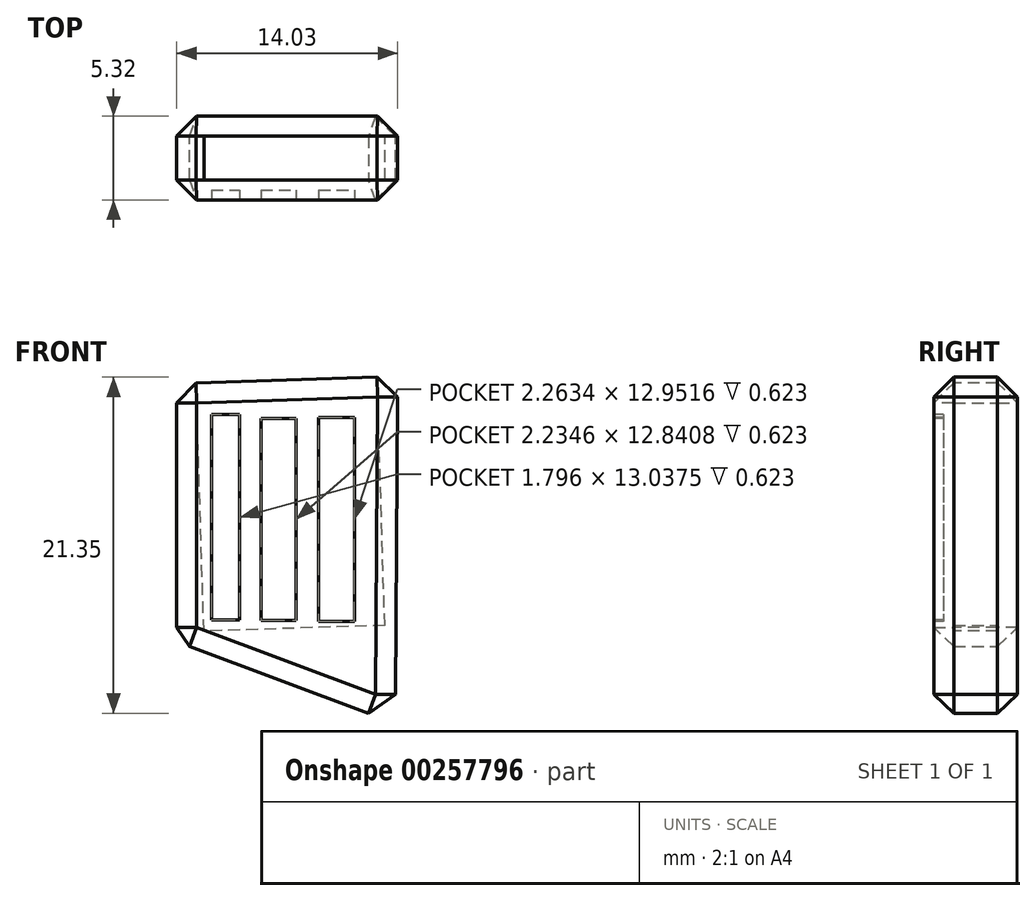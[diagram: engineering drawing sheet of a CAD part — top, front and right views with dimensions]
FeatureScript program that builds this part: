
annotation { "Feature Type Name" : "Feature", "Feature Type Description" : "" }
export const myFeature = defineFeature(function(context is Context, id is Id, definition is map)
    precondition{}
    {
        {
            var Q0;
            Q0=qCreatedBy(makeId("Front.planeOp"),FACE);
            var sketch = newSketch(context, id + "F4", { "sketchPlane" : qUnion([Q0])});
            skLineSegment(sketch, "E0", {"start": v(-13.89, 0) * mm, "end": v(-13.89, -16.38) * mm});
            skLineSegment(sketch, "E1", {"start": v(-13.89, -16.38) * mm, "end": v(0, -21.59) * mm});
            skLineSegment(sketch, "E2", {"start": v(0, -21.59) * mm, "end": v(0.15, 0.44) * mm});
            skLineSegment(sketch, "E3", {"start": v(0.15, 0.44) * mm, "end": v(-13.89, 0) * mm});
            skSolve(sketch);
        }
        {
            var Q0;
            Q0=qSketchRegion(id+"F4",true);
            extrude(context, id + "F0", {"entities" : qUnion([Q0]), "depth" : 5.32 * mm});
        }
        {
            var Q0;
            Q0=makeQuery(id+"F0.opExtrude","CAP_EDGE",EDGE,{"disambiguationData":[OSD([sQuery(id+"F4.wireOp",EDGE,"E0")])],"isStart":false});
            var Q1;
            Q1=makeQuery(id+"F0.opExtrude","CAP_EDGE",EDGE,{"disambiguationData":[OSD([sQuery(id+"F4.wireOp",EDGE,"E3")])],"isStart":false});
            var Q2;
            Q2=makeQuery(id+"F0.opExtrude","CAP_EDGE",EDGE,{"disambiguationData":[OSD([sQuery(id+"F4.wireOp",EDGE,"E1")])],"isStart":false});
            var Q3;
            Q3=makeQuery(id+"F0.opExtrude","CAP_EDGE",EDGE,{"disambiguationData":[OSD([sQuery(id+"F4.wireOp",EDGE,"E2")])],"isStart":false});
            var Q4;
            Q4=makeQuery(id+"F0.opExtrude","SWEPT_EDGE",EDGE,{"disambiguationData":[OSD([sQuery(id+"F4.wireOp",EDGE,"E1"),sQuery(id+"F4.wireOp",EDGE,"E2")])]});
            var Q5;
            Q5=makeQuery(id+"F0.opExtrude","SWEPT_EDGE",EDGE,{"disambiguationData":[OSD([sQuery(id+"F4.wireOp",EDGE,"E0"),sQuery(id+"F4.wireOp",EDGE,"E1")])]});
            var Q6;
            Q6=makeQuery(id+"F0.opExtrude","CAP_EDGE",EDGE,{"disambiguationData":[OSD([sQuery(id+"F4.wireOp",EDGE,"E1")])],"isStart":true});
            var Q7;
            Q7=makeQuery(id+"F0.opExtrude","CAP_EDGE",EDGE,{"disambiguationData":[OSD([sQuery(id+"F4.wireOp",EDGE,"E0")])],"isStart":true});
            var Q8;
            Q8=makeQuery(id+"F0.opExtrude","SWEPT_EDGE",EDGE,{"disambiguationData":[OSD([sQuery(id+"F4.wireOp",EDGE,"E0"),sQuery(id+"F4.wireOp",EDGE,"E3")])]});
            var Q9;
            Q9=makeQuery(id+"F0.opExtrude","CAP_EDGE",EDGE,{"disambiguationData":[OSD([sQuery(id+"F4.wireOp",EDGE,"E3")])],"isStart":true});
            var Q10;
            Q10=makeQuery(id+"F0.opExtrude","SWEPT_EDGE",EDGE,{"disambiguationData":[OSD([sQuery(id+"F4.wireOp",EDGE,"E2"),sQuery(id+"F4.wireOp",EDGE,"E3")])]});
            var Q11;
            Q11=makeQuery(id+"F0.opExtrude","CAP_EDGE",EDGE,{"disambiguationData":[OSD([sQuery(id+"F4.wireOp",EDGE,"E2")])],"isStart":true});
            chamfer(context, id + "F1", {"entities" : qUnion([Q0, Q1, Q2, Q3, Q4, Q5, Q6, Q7, Q8, Q9, Q10, Q11]), "width" : 1.27 * mm, "tangentPropagation" : true});
        }
        {
            var Q0;
            Q0=makeQuery(id+"F0.opExtrude","SWEPT_FACE",FACE,{"disambiguationData":[OSD([sQuery(id+"F4.wireOp",EDGE,"E3")])]});
            extrude(context, id + "F5", {"entities" : qUnion([Q0]), "operationType" : NewBodyOperationType.REMOVE, "oppositeDirection" : true, "depth" : 15.78 * mm});
        }
        {
            var Q0;
            Q0=makeQuery(id+"F0.opExtrude","CAP_FACE",FACE,{"disambiguationData":[OSD([sQuery(id+"F4.wireOp",EDGE,"E0"),sQuery(id+"F4.wireOp",EDGE,"E1"),sQuery(id+"F4.wireOp",EDGE,"E2"),sQuery(id+"F4.wireOp",EDGE,"E3")])],"isStart":false});
            var sketch = newSketch(context, id + "F2", { "sketchPlane" : qUnion([Q0])});
            skLineSegment(sketch, "E4.bottom", {"start": v(-11.68, -1.98) * mm, "end": v(-9.88, -1.98) * mm});
            skLineSegment(sketch, "E4.top", {"start": v(-11.68, -15.02) * mm, "end": v(-9.88, -15.02) * mm});
            skLineSegment(sketch, "E4.left", {"start": v(-11.68, -1.98) * mm, "end": v(-11.68, -15.02) * mm});
            skLineSegment(sketch, "E4.right", {"start": v(-9.88, -1.98) * mm, "end": v(-9.88, -15.02) * mm});
            skLineSegment(sketch, "E5.bottom", {"start": v(-8.54, -2.22) * mm, "end": v(-6.3, -2.22) * mm});
            skLineSegment(sketch, "E5.top", {"start": v(-8.54, -15.06) * mm, "end": v(-6.3, -15.06) * mm});
            skLineSegment(sketch, "E5.left", {"start": v(-8.54, -2.22) * mm, "end": v(-8.54, -15.06) * mm});
            skLineSegment(sketch, "E5.right", {"start": v(-6.3, -2.22) * mm, "end": v(-6.3, -15.06) * mm});
            skLineSegment(sketch, "E6.bottom", {"start": v(-4.87, -2.15) * mm, "end": v(-2.6, -2.15) * mm});
            skLineSegment(sketch, "E6.top", {"start": v(-4.87, -15.1) * mm, "end": v(-2.6, -15.1) * mm});
            skLineSegment(sketch, "E6.left", {"start": v(-4.87, -2.15) * mm, "end": v(-4.87, -15.1) * mm});
            skLineSegment(sketch, "E6.right", {"start": v(-2.6, -2.15) * mm, "end": v(-2.6, -15.1) * mm});
            skSolve(sketch);
        }
        {
            var Q0;
            Q0=qSketchRegion(id+"F2",true);
            extrude(context, id + "F3", {"entities" : qUnion([Q0]), "operationType" : NewBodyOperationType.REMOVE, "oppositeDirection" : true, "depth" : 0.62 * mm});
        }
    });
